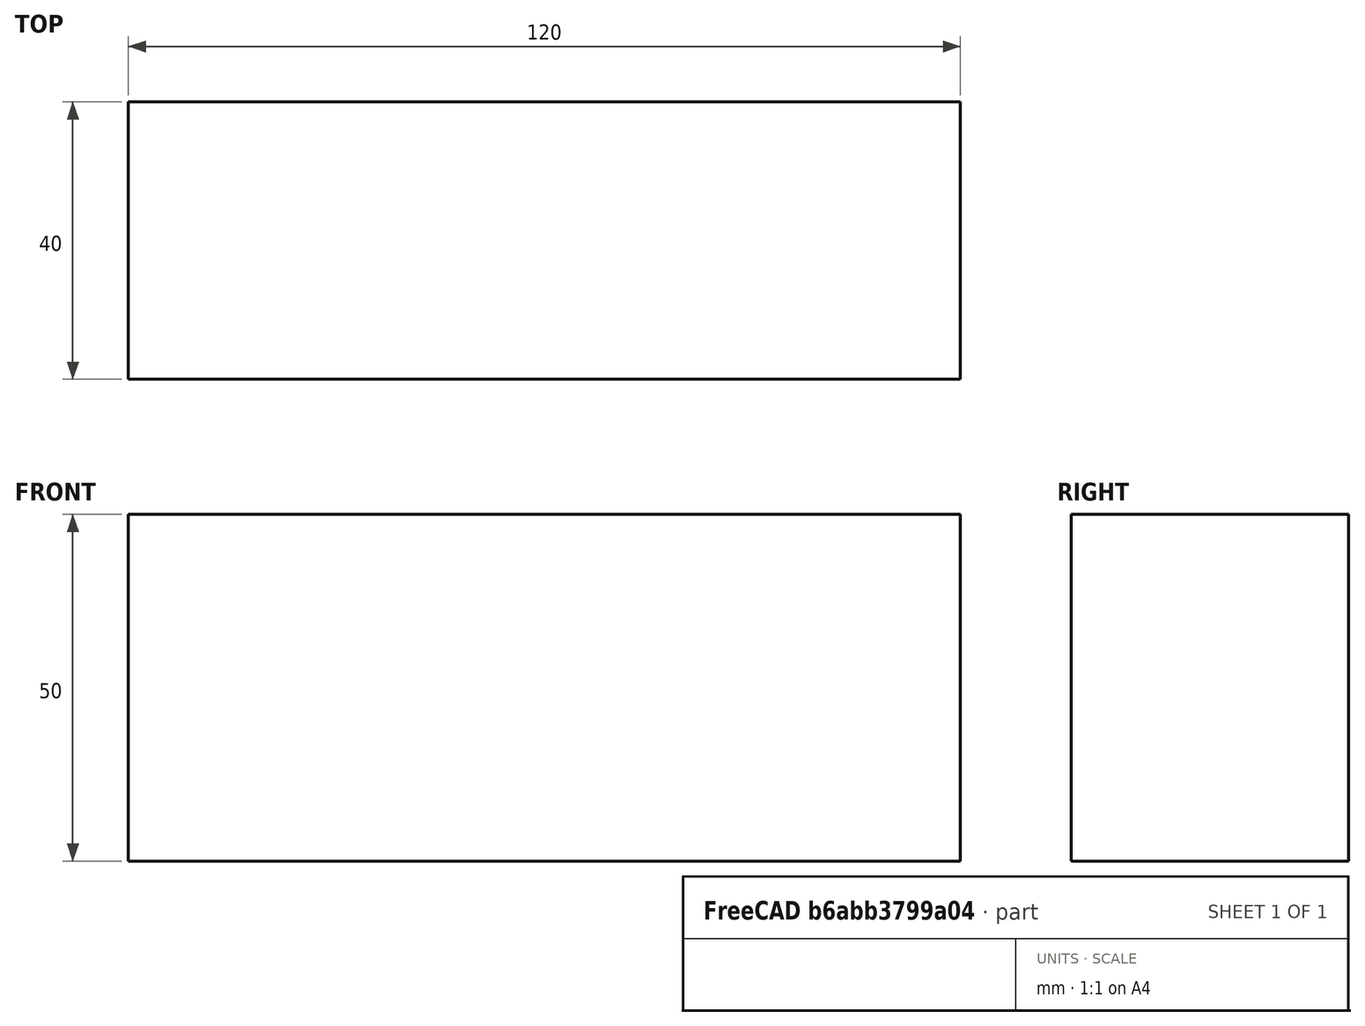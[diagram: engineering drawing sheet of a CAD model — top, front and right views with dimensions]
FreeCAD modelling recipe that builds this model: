
FCSTD DOCUMENT  (FreeCAD 0.15R4671 (Git))
Label: Flat Bar 120x40 EN10058 S235JR
License: All rights reserved
LicenseURL: http://en.wikipedia.org/wiki/All_rights_reserved
objects: Sketcher::SketchObject×1, Part::Extrusion×1
note: 2 computed .brp shape members not serialized (recipe doc carries the construction recipe); baked Part::Feature solids carry a one-line shape summary decoded from their .brp

FEATURE [Sketcher::SketchObject] Sketch
  sketch-geometry (4):
    g0: LineSegment StartX=-60 StartY=-20 StartZ=0 EndX=60 EndY=-20 EndZ=0
    g1: LineSegment StartX=60 StartY=-20 StartZ=0 EndX=60 EndY=20 EndZ=0
    g2: LineSegment StartX=60 StartY=20 StartZ=0 EndX=-60 EndY=20 EndZ=0
    g3: LineSegment StartX=-60 StartY=20 StartZ=0 EndX=-60 EndY=-20 EndZ=0
  constraints (12):
    c: Coincident(g0,g1)
    c: Coincident(g1,g2)
    c: Coincident(g2,g3)
    c: Coincident(g3,g0)
    c: Horizontal(g0)
    c: Horizontal(g2)
    c: Vertical(g1)
    c: Vertical(g3)
    c: Symmetric(g1,g2,g-2)
    c: Symmetric(g0,g1,g-1)
    c: DistanceY(g1) = 40
    c: DistanceX(g0) = 120
FEATURE [Part::Extrusion] Extrude  label="Flat Bar 120x40 EN10058 S235JR"
  Base = -> Sketch
  Dir = (0,0,50)
  Solid = true
